# Revit family: Door-Exterior-Simpson-Traditional-6_Panel
name_source: partatom
category: Doors
revit_build: Autodesk Revit Architecture 2012 (Build: 20110916_2132(x64)
units: mm (PartAtom-declared; Revit-internal decimal feet)

## types (1)
- Door-Exterior-Simpson-Traditional-6_Panel
    Assembly Code = B2030230
    Bottom Rail Height = 8 11/16"
    Default Sill Height = 0"
    Description = Door
    Frame = Wood - Simpson Doors - Douglas Fir
    Frame Width = 3"
    Function = Exterior
    Glass = Glass - Simpson Doors - Clear
    Glass Options = http://simpsondoor.com
    Glass Thickness = 3/4"
    Height = 84"
    Horizontal Divider Width = 3 1/2"
    Lock Rail Height = 6 1/2"
    Lower Panel Height = 24"
    Manufacturer = Simpson Door Company
    Model = 6173
    Notes = Dozens of glass textures and colors are available. For a list of standard options visit the Simpson web site or submit a custom glass request.
    Panel = Wood - Simpson Doors - Douglas Fir
    Panel Insert Type = Traditional-6_Panel : 2 Lite
    Panel Stile Width = 4"
    Panel Thickness = 3/4"
    Product Documentation Link = http://www.simpsondoor.com
    Product Page URL = http://www.simpsondoor.com
    Rough Height = 81"
    Rough Width = 20"
    Thickness = 1 3/4"
    Top Rail Height = 3 15/16"
    Top Secondary Panel Height = 9 3/8"
    URL = http://www.simpsondoor.com
    UltraBlock Note = This Door Comes with The Option of UltraBlock Technology. It is Turn On as a Default
    UltraBlock Option = Yes
    Vertical Divider Width = 3 1/2"
    Wall Closure = By host
    WaterBarrier Note = This Door Comes with The Option of WaterBarrier with UltraBlock Technology. It is Turn Off as a Default
    WaterBarrier with UltraBlock Technology = No
    Width = 26"
    Wood Species = http://simpsondoor.com
    Wood Species Note = Available in Any Wood Species

## geometry (parser evidence)
native form markers: Blend x24, Sweep x40
no freeform markers — native parametric forms only
